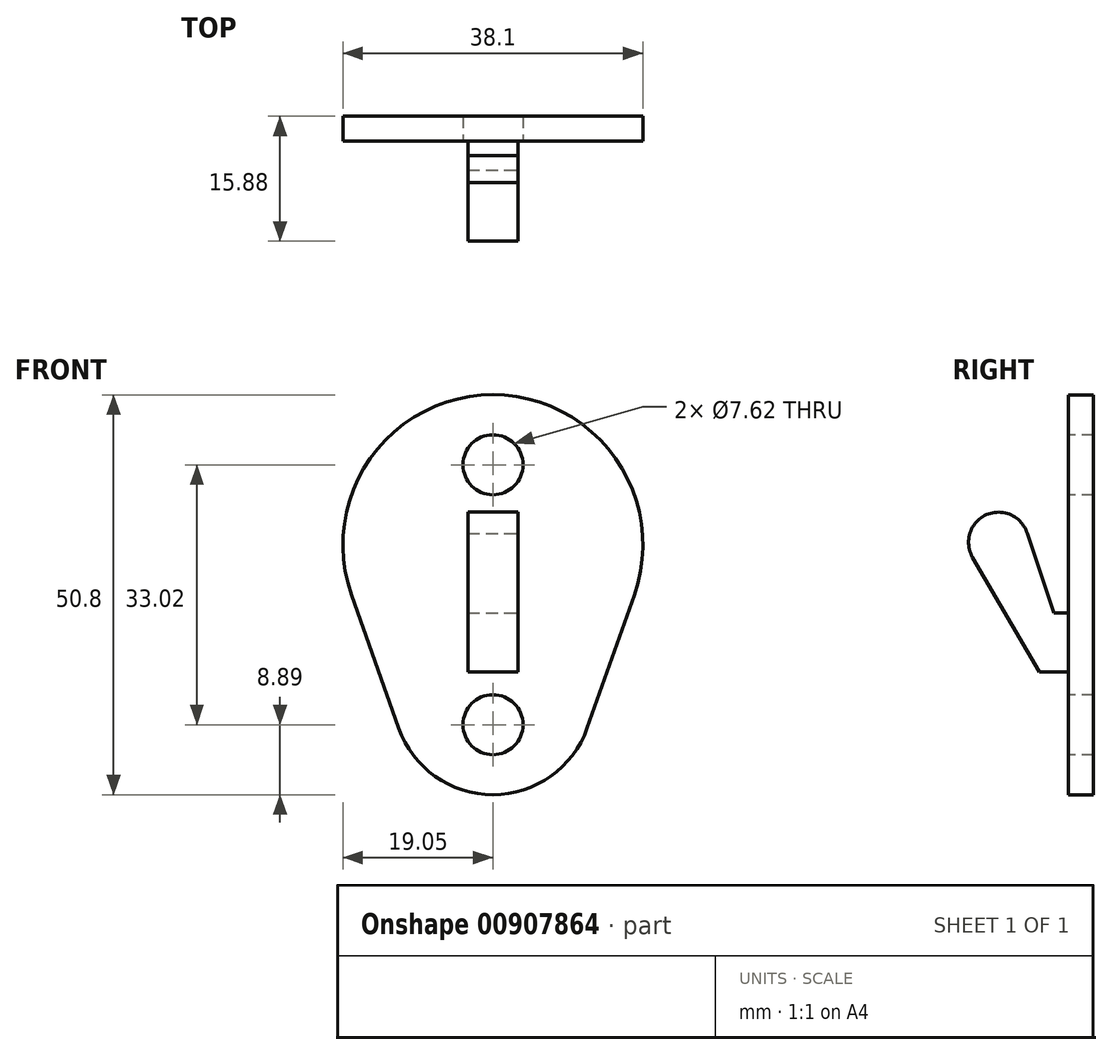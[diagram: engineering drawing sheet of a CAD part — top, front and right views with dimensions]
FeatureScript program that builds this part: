
annotation { "Feature Type Name" : "Feature", "Feature Type Description" : "" }
export const myFeature = defineFeature(function(context is Context, id is Id, definition is map)
    precondition{}
    {
        {
            var Q0;
            Q0=qCreatedBy(makeId("Front.planeOp"),FACE);
            var sketch = newSketch(context, id + "F0", { "sketchPlane" : qUnion([Q0])});
            skArc(sketch, "E0", {"start": v(-11.97, -27.41) * mm, "mid": v(0, -35.88) * mm, "end": v(11.97, -27.41) * mm});
            skArc(sketch, "E1", {"start": v(17.96, -10.48) * mm, "mid": v(0, 14.92) * mm, "end": v(-17.96, -10.48) * mm});
            skLineSegment(sketch, "E2", {"start": v(-17.96, -10.48) * mm, "end": v(-11.97, -27.41) * mm});
            skLineSegment(sketch, "E3", {"start": v(11.97, -27.41) * mm, "end": v(17.96, -10.48) * mm});
            skSolve(sketch);
        }
        {
            var Q0;
            Q0 = qSketchRegion(id + "F0", true);
            extrude(context, id + "F1", {"entities" : qUnion([Q0]), "depth" : 3.17 * mm, "offsetDistance" : 25.4 * mm});
        }
        {
            var Q0;
            Q0=makeQuery(id+"F1.opExtrude","CAP_FACE",FACE,{"disambiguationData":[OSD([sQuery(id+"F0.wireOp",EDGE,"E0"),sQuery(id+"F0.wireOp",EDGE,"E1"),sQuery(id+"F0.wireOp",EDGE,"E2"),sQuery(id+"F0.wireOp",EDGE,"E3")])],"isStart":false});
            var sketch = newSketch(context, id + "F2", { "sketchPlane" : qUnion([Q0])});
            skCircle(sketch, "E4", {"center": v(0, 6.03) * mm, "radius": 3.81 * mm});
            skCircle(sketch, "E5", {"center": v(0, -27) * mm, "radius": 3.81 * mm});
            skSolve(sketch);
        }
        {
            var Q0;
            Q0 = qSketchRegion(id + "F2", true);
            extrude(context, id + "F3", {"entities" : qUnion([Q0]), "operationType" : NewBodyOperationType.REMOVE, "oppositeDirection" : true, "depth" : 25.4 * mm, "offsetDistance" : 25.4 * mm});
        }
        {
            var Q0;
            Q0=qCreatedBy(makeId("Right.planeOp"),FACE);
            cPlane(context, id + "F4", {"entities" : qUnion([Q0]), "cplaneType" : CPlaneType.OFFSET, "offset" : 3.17 * mm, "width" : 152.4 * mm, "height" : 152.4 * mm});
        }
        {
            var Q0;
            Q0=qCreatedBy(id+"F4.planeOp",FACE);
            var sketch = newSketch(context, id + "F5", { "sketchPlane" : qUnion([Q0])});
            skLineSegment(sketch, "E6", {"start": v(-6.86, -20.32) * mm, "end": v(-3.17, -20.32) * mm});
            skLineSegment(sketch, "E7", {"start": v(-3.17, -20.32) * mm, "end": v(-3.17, -12.83) * mm});
            skArc(sketch, "E8", {"start": v(-8.42, -2.7) * mm, "mid": v(-13.59, -0.32) * mm, "end": v(-15.36, -5.73) * mm});
            skLineSegment(sketch, "E9", {"start": v(-3.17, -12.83) * mm, "end": v(-5.02, -12.83) * mm});
            skLineSegment(sketch, "E10", {"start": v(-3.17, -20.32) * mm, "end": v(-6.86, -20.32) * mm});
            skLineSegment(sketch, "E11", {"start": v(-6.86, -20.32) * mm, "end": v(-15.36, -5.73) * mm});
            skLineSegment(sketch, "E12", {"start": v(-8.42, -2.7) * mm, "end": v(-5.02, -12.83) * mm});
            skPoint(sketch, "E13.orphan", {"position": v(-6.86, -12.83) * mm});
            skPoint(sketch, "E14.orphan", {"position": v(-3.18, 0) * mm});
            skSolve(sketch);
        }
        {
            var Q0;
            Q0 = qSketchRegion(id + "F5", true);
            extrude(context, id + "F6", {"entities" : qUnion([Q0]), "operationType" : NewBodyOperationType.ADD, "oppositeDirection" : true, "depth" : 6.35 * mm, "offsetDistance" : 25.4 * mm});
        }
    });
